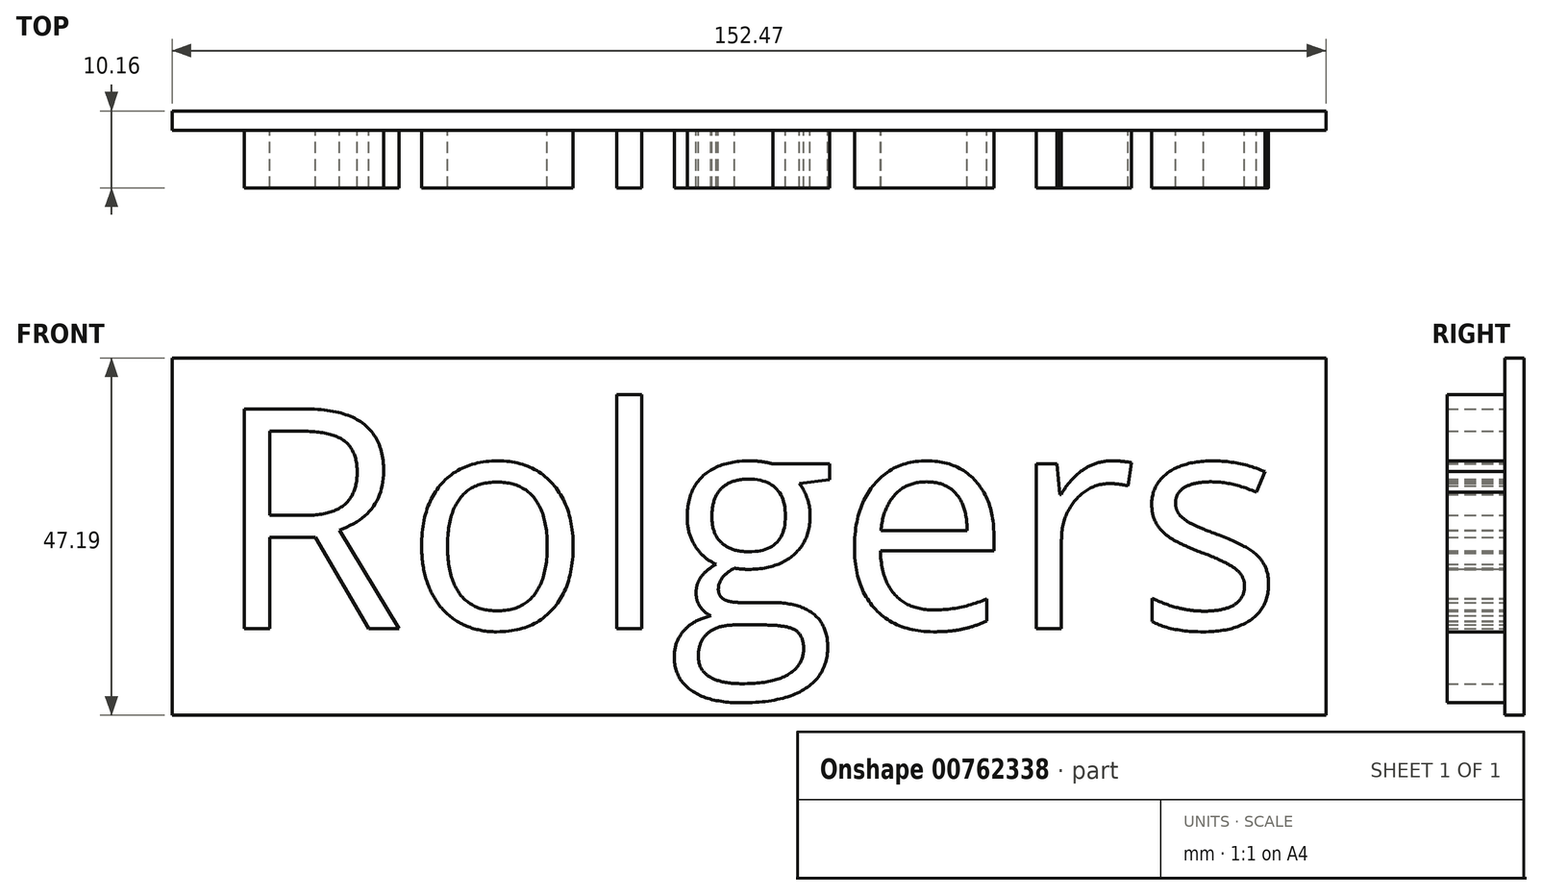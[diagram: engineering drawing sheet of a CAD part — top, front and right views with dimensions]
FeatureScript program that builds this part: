
annotation { "Feature Type Name" : "Feature", "Feature Type Description" : "" }
export const myFeature = defineFeature(function(context is Context, id is Id, definition is map)
    precondition{}
    {
        {
            var Q0;
            Q0=qCreatedBy(makeId("Front.planeOp"),FACE);
            var sketch = newSketch(context, id + "F0", { "sketchPlane" : qUnion([Q0])});
            skLineSegment(sketch, "E0.bottom", {"start": v(-76.25, -7.65) * mm, "end": v(76.22, -7.65) * mm});
            skLineSegment(sketch, "E0.top", {"start": v(-76.25, 39.54) * mm, "end": v(76.22, 39.54) * mm});
            skLineSegment(sketch, "E0.left", {"start": v(-76.25, -7.65) * mm, "end": v(-76.25, 39.54) * mm});
            skLineSegment(sketch, "E0.right", {"start": v(76.22, -7.65) * mm, "end": v(76.22, 39.54) * mm});
            skSolve(sketch);
        }
        {
            var Q0;
            Q0 = qSketchRegion(id + "F0", true);
            extrude(context, id + "F1", {"entities" : qUnion([Q0]), "depth" : 2.54 * mm, "offsetDistance" : 25.4 * mm});
        }
        {
            var Q0;
            Q0=makeQuery(id+"F1.opExtrude","CAP_FACE",FACE,{"disambiguationData":[OSD([sQuery(id+"F0.wireOp",EDGE,"E0.bottom"),sQuery(id+"F0.wireOp",EDGE,"E0.top"),sQuery(id+"F0.wireOp",EDGE,"E0.left"),sQuery(id+"F0.wireOp",EDGE,"E0.right")])],"isStart":false});
            var sketch = newSketch(context, id + "F2", { "sketchPlane" : qUnion([Q0])});
            skText(sketch, "E1", { "text": "Rolgers\n", "fontName": "OpenSans-Regular.ttf"});
            const initialGuessF2  = {"E1": [-0.07072, 0.00378, 1, 0, 0.02931]};
            skSetInitialGuess(sketch, initialGuessF2);
            skSolve(sketch);
        }
        {
            var Q0;
            Q0 = qSketchRegion(id + "F2", true);
            extrude(context, id + "F3", {"entities" : qUnion([Q0]), "operationType" : NewBodyOperationType.ADD, "depth" : 7.62 * mm, "offsetDistance" : 25.4 * mm});
        }
    });
